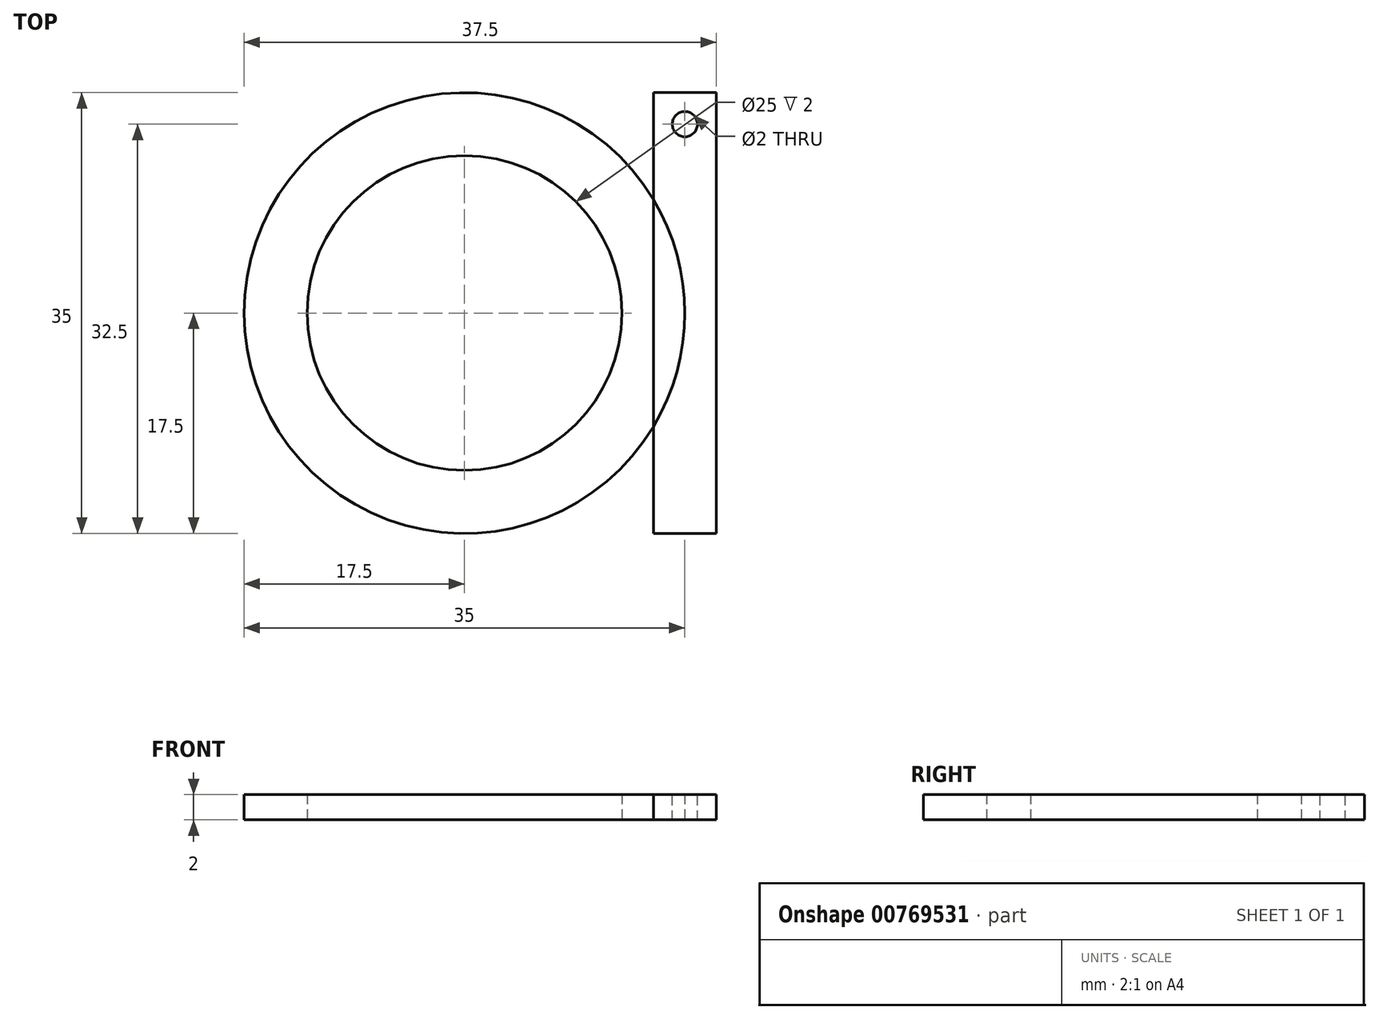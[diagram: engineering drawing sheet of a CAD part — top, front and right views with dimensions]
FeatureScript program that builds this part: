
annotation { "Feature Type Name" : "Feature", "Feature Type Description" : "" }
export const myFeature = defineFeature(function(context is Context, id is Id, definition is map)
    precondition{}
    {
        {
            var Q0;
            Q0=qCreatedBy(makeId("Top.planeOp"),FACE);
            var sketch = newSketch(context, id + "F0", { "sketchPlane" : qUnion([Q0])});
            skCircle(sketch, "E0", {"center": v(0, 0) * mm, "radius": 17.5 * mm});
            skCircle(sketch, "E1", {"center": v(0, 0) * mm, "radius": 12.5 * mm});
            skLineSegment(sketch, "E2.bottom", {"start": v(15, 17.5) * mm, "end": v(20, 17.5) * mm});
            skLineSegment(sketch, "E2.top", {"start": v(15, -17.5) * mm, "end": v(20, -17.5) * mm});
            skLineSegment(sketch, "E2.left", {"start": v(15, 17.5) * mm, "end": v(15, -17.5) * mm});
            skLineSegment(sketch, "E2.right", {"start": v(20, 17.5) * mm, "end": v(20, -17.5) * mm});
            skSolve(sketch);
        }
        {
            var Q0;
            Q0=makeQuery(id+"F0.imprint","IMPRINT",FACE,{"disambiguationData":[TD([[makeQuery(id+"F0.imprint","IMPRINT",EDGE,{"derivedFrom":sQuery(id+"F0.wireOp",EDGE,"E1")}),-1.0]])]});
            var Q1;
            {var subQ1=sQuery(id+"F0.wireOp",EDGE,"E2.bottom");Q1=makeQuery(id+"F0.imprint","IMPRINT",FACE,{"disambiguationData":[TD([[makeQuery(id+"F0.imprint","IMPRINT",EDGE,{"derivedFrom":subQ1}),-1.0]])]});}
            var Q2;
            {var subQ0=sQuery(id+"F0.wireOp",EDGE,"E2.left");var subQ1=sQuery(id+"F0.wireOp",EDGE,"E0");var subQ2=makeQuery(id+"F0.imprint","INTERSECT",VERTEX,{"disambiguationData":[OD(0.0)],"derivedFrom":[subQ1,subQ0]});Q2=makeQuery(id+"F0.imprint","IMPRINT",FACE,{"disambiguationData":[TD([[makeQuery(id+"F0.imprint","IMPRINT",EDGE,{"disambiguationData":[TD([[subQ2,1.0]])],"derivedFrom":subQ1}),1.0]])]});}
            extrude(context, id + "F1", {"entities" : qUnion([Q0, Q1, Q2]), "depth" : 2 * mm, "offsetDistance" : 25 * mm});
        }
        {
            var Q0;
            Q0=makeQuery(id+"F1.opExtrude","CAP_FACE",FACE,{"disambiguationData":[OSD([sQuery(id+"F0.wireOp",EDGE,"E0"),sQuery(id+"F0.wireOp",EDGE,"E1"),sQuery(id+"F0.wireOp",EDGE,"E2.bottom"),sQuery(id+"F0.wireOp",EDGE,"E2.top"),sQuery(id+"F0.wireOp",EDGE,"E2.left"),sQuery(id+"F0.wireOp",EDGE,"E2.right")])],"isStart":false});
            var sketch = newSketch(context, id + "F2", { "sketchPlane" : qUnion([Q0])});
            skCircle(sketch, "E3", {"center": v(17.5, 15) * mm, "radius": 1 * mm});
            skSolve(sketch);
        }
        {
            var Q0;
            Q0=makeQuery(id+"F2.imprint","IMPRINT",FACE,{"disambiguationData":[TD([[makeQuery(id+"F2.imprint","IMPRINT",EDGE,{"derivedFrom":sQuery(id+"F2.wireOp",EDGE,"E3")}),1.0]])]});
            extrude(context, id + "F3", {"entities" : qUnion([Q0]), "operationType" : NewBodyOperationType.REMOVE, "oppositeDirection" : true, "depth" : 2 * mm, "offsetDistance" : 25 * mm});
        }
    });
